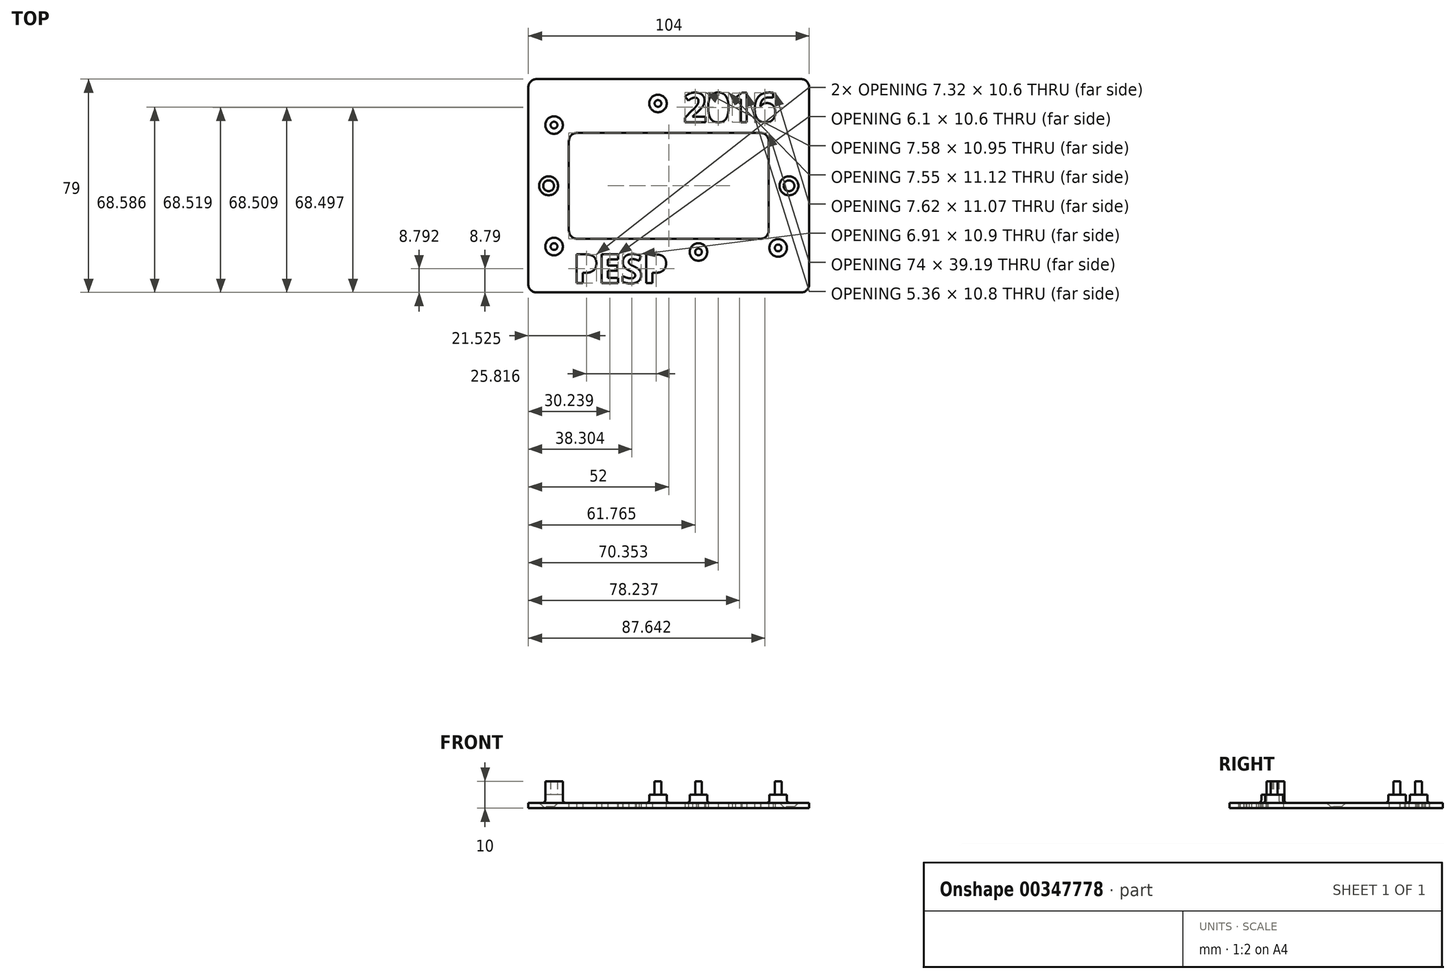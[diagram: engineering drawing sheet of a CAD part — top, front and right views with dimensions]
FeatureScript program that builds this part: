
annotation { "Feature Type Name" : "Feature", "Feature Type Description" : "" }
export const myFeature = defineFeature(function(context is Context, id is Id, definition is map)
    precondition{}
    {
        {
            var Q0;
            Q0=qCreatedBy(makeId("Top.planeOp"),FACE);
            var sketch = newSketch(context, id + "F0", { "sketchPlane" : qUnion([Q0])});
            skLineSegment(sketch, "E0.bottom", {"start": v(47, -34.5) * mm, "end": v(-47, -34.5) * mm});
            skLineSegment(sketch, "E0.top", {"start": v(47, 34.5) * mm, "end": v(-47, 34.5) * mm});
            skLineSegment(sketch, "E0.left", {"start": v(47, -34.5) * mm, "end": v(47, 34.5) * mm});
            skLineSegment(sketch, "E0.right", {"start": v(-47, -34.5) * mm, "end": v(-47, 34.5) * mm});
            skPoint(sketch, "E0.middle", {"position": v(0, 0) * mm});
            skLineSegment(sketch, "E1.0", {"start": v(52, 39.5) * mm, "end": v(-52, 39.5) * mm});
            skLineSegment(sketch, "E1.1", {"start": v(52, -39.5) * mm, "end": v(52, 39.5) * mm});
            skLineSegment(sketch, "E1.2", {"start": v(52, -39.5) * mm, "end": v(-52, -39.5) * mm});
            skLineSegment(sketch, "E1.3", {"start": v(-52, -39.5) * mm, "end": v(-52, 39.5) * mm});
            skCircle(sketch, "E2", {"center": v(-42.5, 22.5) * mm, "radius": 1.25 * mm});
            skCircle(sketch, "E3.MirrorC", {"center": v(-42.5, -22.5) * mm, "radius": 1.25 * mm});
            skCircle(sketch, "E4", {"center": v(-4, 30.5) * mm, "radius": 1.25 * mm});
            skCircle(sketch, "E5", {"center": v(40.5, -23) * mm, "radius": 1.25 * mm});
            skCircle(sketch, "E6", {"center": v(11, -24.5) * mm, "radius": 1.25 * mm});
            skCircle(sketch, "E7.0", {"center": v(-4, 30.5) * mm, "radius": 3.25 * mm});
            skCircle(sketch, "E8.0", {"center": v(-42.5, 22.5) * mm, "radius": 3.25 * mm});
            skCircle(sketch, "E9.0", {"center": v(11, -24.5) * mm, "radius": 3.25 * mm});
            skCircle(sketch, "E10.0", {"center": v(40.5, -23) * mm, "radius": 3.25 * mm});
            skCircle(sketch, "E11.MirrorC", {"center": v(-42.5, -22.5) * mm, "radius": 3.25 * mm});
            skLineSegment(sketch, "E12.bottom", {"start": v(-37, 19.6) * mm, "end": v(37, 19.6) * mm});
            skLineSegment(sketch, "E12.top", {"start": v(-37, -19.6) * mm, "end": v(37, -19.6) * mm});
            skLineSegment(sketch, "E12.left", {"start": v(-37, 19.6) * mm, "end": v(-37, -19.6) * mm});
            skLineSegment(sketch, "E12.right", {"start": v(37, 19.6) * mm, "end": v(37, -19.6) * mm});
            skText(sketch, "E13", { "text": "PESP", "fontName": "OpenSans-Bold.ttf"});
            skText(sketch, "E14", { "text": "2016", "fontName": "OpenSans-Bold.ttf"});
            skCircle(sketch, "E15", {"center": v(-44.5, 0) * mm, "radius": 2 * mm});
            skCircle(sketch, "E16.MirrorC", {"center": v(44.5, 0) * mm, "radius": 2 * mm});
            const initialGuessF0  = {"E13": [-0.03547, -0.03601, 1, 0, 0.01069], "E14": [0.0054, 0.02361, 1, 0, 0.01089]};
            skSetInitialGuess(sketch, initialGuessF0);
            skSolve(sketch);
        }
        {
            var Q0;
            Q0=makeQuery(id+"F0.imprint","IMPRINT",FACE,{"disambiguationData":[TD([[makeQuery(id+"F0.imprint","IMPRINT",EDGE,{"derivedFrom":sQuery(id+"F0.wireOp",EDGE,"E0.bottom")}),1.0]])]});
            var Q1;
            Q1=makeQuery(id+"F0.imprint","IMPRINT",FACE,{"disambiguationData":[TD([[makeQuery(id+"F0.imprint","IMPRINT",EDGE,{"derivedFrom":sQuery(id+"F0.wireOp",EDGE,"E0.bottom")}),-1.0]])]});
            var Q2;
            Q2=makeQuery(id+"F0.imprint","IMPRINT",FACE,{"disambiguationData":[TD([[makeQuery(id+"F0.imprint","IMPRINT",EDGE,{"derivedFrom":sQuery(id+"F0.wireOp",EDGE,"E4")}),-1.0]])]});
            var Q3;
            Q3=makeQuery(id+"F0.imprint","IMPRINT",FACE,{"disambiguationData":[TD([[makeQuery(id+"F0.imprint","IMPRINT",EDGE,{"derivedFrom":sQuery(id+"F0.wireOp",EDGE,"E4")}),1.0]])]});
            var Q4;
            Q4=makeQuery(id+"F0.imprint","IMPRINT",FACE,{"disambiguationData":[TD([[makeQuery(id+"F0.imprint","IMPRINT",EDGE,{"derivedFrom":sQuery(id+"F0.wireOp",EDGE,"E5")}),1.0]])]});
            var Q5;
            Q5=makeQuery(id+"F0.imprint","IMPRINT",FACE,{"disambiguationData":[TD([[makeQuery(id+"F0.imprint","IMPRINT",EDGE,{"derivedFrom":sQuery(id+"F0.wireOp",EDGE,"E5")}),-1.0]])]});
            var Q6;
            Q6=makeQuery(id+"F0.imprint","IMPRINT",FACE,{"disambiguationData":[TD([[makeQuery(id+"F0.imprint","IMPRINT",EDGE,{"derivedFrom":sQuery(id+"F0.wireOp",EDGE,"E6")}),1.0]])]});
            var Q7;
            Q7=makeQuery(id+"F0.imprint","IMPRINT",FACE,{"disambiguationData":[TD([[makeQuery(id+"F0.imprint","IMPRINT",EDGE,{"derivedFrom":sQuery(id+"F0.wireOp",EDGE,"E6")}),-1.0]])]});
            var Q8;
            Q8=makeQuery(id+"F0.imprint","IMPRINT",FACE,{"disambiguationData":[TD([[makeQuery(id+"F0.imprint","IMPRINT",EDGE,{"derivedFrom":sQuery(id+"F0.wireOp",EDGE,"E3.MirrorC")}),-1.0]])]});
            var Q9;
            Q9=makeQuery(id+"F0.imprint","IMPRINT",FACE,{"disambiguationData":[TD([[makeQuery(id+"F0.imprint","IMPRINT",EDGE,{"derivedFrom":sQuery(id+"F0.wireOp",EDGE,"E3.MirrorC")}),1.0]])]});
            var Q10;
            Q10=makeQuery(id+"F0.imprint","IMPRINT",FACE,{"disambiguationData":[TD([[makeQuery(id+"F0.imprint","IMPRINT",EDGE,{"derivedFrom":sQuery(id+"F0.wireOp",EDGE,"E2")}),-1.0]])]});
            var Q11;
            Q11=makeQuery(id+"F0.imprint","IMPRINT",FACE,{"disambiguationData":[TD([[makeQuery(id+"F0.imprint","IMPRINT",EDGE,{"derivedFrom":sQuery(id+"F0.wireOp",EDGE,"E2")}),1.0]])]});
            extrude(context, id + "F1", {"entities" : qUnion([Q0, Q1, Q2, Q3, Q4, Q5, Q6, Q7, Q8, Q9, Q10, Q11]), "depth" : 2 * mm});
        }
        {
            var Q0;
            Q0=makeQuery(id+"F0.imprint","IMPRINT",FACE,{"disambiguationData":[TD([[makeQuery(id+"F0.imprint","IMPRINT",EDGE,{"derivedFrom":sQuery(id+"F0.wireOp",EDGE,"E4")}),1.0]])]});
            var Q1;
            Q1=makeQuery(id+"F0.imprint","IMPRINT",FACE,{"disambiguationData":[TD([[makeQuery(id+"F0.imprint","IMPRINT",EDGE,{"derivedFrom":sQuery(id+"F0.wireOp",EDGE,"E4")}),-1.0]])]});
            var Q2;
            Q2=makeQuery(id+"F0.imprint","IMPRINT",FACE,{"disambiguationData":[TD([[makeQuery(id+"F0.imprint","IMPRINT",EDGE,{"derivedFrom":sQuery(id+"F0.wireOp",EDGE,"E3.MirrorC")}),-1.0]])]});
            var Q3;
            Q3=makeQuery(id+"F0.imprint","IMPRINT",FACE,{"disambiguationData":[TD([[makeQuery(id+"F0.imprint","IMPRINT",EDGE,{"derivedFrom":sQuery(id+"F0.wireOp",EDGE,"E3.MirrorC")}),1.0]])]});
            var Q4;
            Q4=makeQuery(id+"F0.imprint","IMPRINT",FACE,{"disambiguationData":[TD([[makeQuery(id+"F0.imprint","IMPRINT",EDGE,{"derivedFrom":sQuery(id+"F0.wireOp",EDGE,"E6")}),1.0]])]});
            var Q5;
            Q5=makeQuery(id+"F0.imprint","IMPRINT",FACE,{"disambiguationData":[TD([[makeQuery(id+"F0.imprint","IMPRINT",EDGE,{"derivedFrom":sQuery(id+"F0.wireOp",EDGE,"E6")}),-1.0]])]});
            var Q6;
            Q6=makeQuery(id+"F0.imprint","IMPRINT",FACE,{"disambiguationData":[TD([[makeQuery(id+"F0.imprint","IMPRINT",EDGE,{"derivedFrom":sQuery(id+"F0.wireOp",EDGE,"E5")}),1.0]])]});
            var Q7;
            Q7=makeQuery(id+"F0.imprint","IMPRINT",FACE,{"disambiguationData":[TD([[makeQuery(id+"F0.imprint","IMPRINT",EDGE,{"derivedFrom":sQuery(id+"F0.wireOp",EDGE,"E5")}),-1.0]])]});
            var Q8;
            Q8=makeQuery(id+"F0.imprint","IMPRINT",FACE,{"disambiguationData":[TD([[makeQuery(id+"F0.imprint","IMPRINT",EDGE,{"derivedFrom":sQuery(id+"F0.wireOp",EDGE,"E2")}),-1.0]])]});
            var Q9;
            Q9=makeQuery(id+"F0.imprint","IMPRINT",FACE,{"disambiguationData":[TD([[makeQuery(id+"F0.imprint","IMPRINT",EDGE,{"derivedFrom":sQuery(id+"F0.wireOp",EDGE,"E2")}),1.0]])]});
            extrude(context, id + "F2", {"entities" : qUnion([Q0, Q1, Q2, Q3, Q4, Q5, Q6, Q7, Q8, Q9]), "operationType" : NewBodyOperationType.ADD, "depth" : 5 * mm});
        }
        {
            var Q0;
            Q0=makeQuery(id+"F0.imprint","IMPRINT",FACE,{"disambiguationData":[TD([[makeQuery(id+"F0.imprint","IMPRINT",EDGE,{"derivedFrom":sQuery(id+"F0.wireOp",EDGE,"E4")}),1.0]])]});
            var Q1;
            Q1=makeQuery(id+"F0.imprint","IMPRINT",FACE,{"disambiguationData":[TD([[makeQuery(id+"F0.imprint","IMPRINT",EDGE,{"derivedFrom":sQuery(id+"F0.wireOp",EDGE,"E2")}),1.0]])]});
            var Q2;
            Q2=makeQuery(id+"F0.imprint","IMPRINT",FACE,{"disambiguationData":[TD([[makeQuery(id+"F0.imprint","IMPRINT",EDGE,{"derivedFrom":sQuery(id+"F0.wireOp",EDGE,"E3.MirrorC")}),-1.0]])]});
            var Q3;
            Q3=makeQuery(id+"F0.imprint","IMPRINT",FACE,{"disambiguationData":[TD([[makeQuery(id+"F0.imprint","IMPRINT",EDGE,{"derivedFrom":sQuery(id+"F0.wireOp",EDGE,"E6")}),1.0]])]});
            var Q4;
            Q4=makeQuery(id+"F0.imprint","IMPRINT",FACE,{"disambiguationData":[TD([[makeQuery(id+"F0.imprint","IMPRINT",EDGE,{"derivedFrom":sQuery(id+"F0.wireOp",EDGE,"E5")}),1.0]])]});
            extrude(context, id + "F3", {"entities" : qUnion([Q0, Q1, Q2, Q3, Q4]), "operationType" : NewBodyOperationType.ADD, "depth" : 10 * mm});
        }
        {
            var Q0;
            Q0=makeQuery(id+"F1.opExtrude","SWEPT_EDGE",EDGE,{"disambiguationData":[OSD([sQuery(id+"F0.wireOp",EDGE,"E12.bottom"),sQuery(id+"F0.wireOp",EDGE,"E12.left")])]});
            var Q1;
            Q1=makeQuery(id+"F1.opExtrude","SWEPT_EDGE",EDGE,{"disambiguationData":[OSD([sQuery(id+"F0.wireOp",EDGE,"E12.bottom"),sQuery(id+"F0.wireOp",EDGE,"E12.right")])]});
            var Q2;
            Q2=makeQuery(id+"F1.opExtrude","SWEPT_EDGE",EDGE,{"disambiguationData":[OSD([sQuery(id+"F0.wireOp",EDGE,"E12.top"),sQuery(id+"F0.wireOp",EDGE,"E12.left")])]});
            var Q3;
            Q3=makeQuery(id+"F1.opExtrude","SWEPT_EDGE",EDGE,{"disambiguationData":[OSD([sQuery(id+"F0.wireOp",EDGE,"E12.top"),sQuery(id+"F0.wireOp",EDGE,"E12.right")])]});
            var Q4;
            Q4=makeQuery(id+"F1.opExtrude","SWEPT_EDGE",EDGE,{"disambiguationData":[OSD([sQuery(id+"F0.wireOp",EDGE,"E1.0"),sQuery(id+"F0.wireOp",EDGE,"E1.1")])]});
            var Q5;
            Q5=makeQuery(id+"F1.opExtrude","SWEPT_EDGE",EDGE,{"disambiguationData":[OSD([sQuery(id+"F0.wireOp",EDGE,"E1.1"),sQuery(id+"F0.wireOp",EDGE,"E1.2")])]});
            var Q6;
            Q6=makeQuery(id+"F1.opExtrude","SWEPT_EDGE",EDGE,{"disambiguationData":[OSD([sQuery(id+"F0.wireOp",EDGE,"E1.0"),sQuery(id+"F0.wireOp",EDGE,"E1.3")])]});
            var Q7;
            Q7=makeQuery(id+"F1.opExtrude","SWEPT_EDGE",EDGE,{"disambiguationData":[OSD([sQuery(id+"F0.wireOp",EDGE,"E1.2"),sQuery(id+"F0.wireOp",EDGE,"E1.3")])]});
            fillet(context, id + "F4", {"entities" : qUnion([Q0, Q1, Q2, Q3, Q4, Q5, Q6, Q7]), "radius" : 3 * mm, "tangentPropagation" : true, "allowEdgeOverflow" : false});
        }
        {
            var Q0;
            Q0=makeQuery(id+"F2.boolean.opBoolean","INTERSECT",EDGE,{"derivedFrom":[makeQuery(id+"F1.opExtrude","CAP_FACE",FACE,{"disambiguationData":[OSD([sQuery(id+"F0.wireOp",EDGE,"E1.0"),sQuery(id+"F0.wireOp",EDGE,"E1.1"),sQuery(id+"F0.wireOp",EDGE,"E1.2"),sQuery(id+"F0.wireOp",EDGE,"E1.3"),sQuery(id+"F0.wireOp",EDGE,"E12.bottom"),sQuery(id+"F0.wireOp",EDGE,"E12.top"),sQuery(id+"F0.wireOp",EDGE,"E12.left"),sQuery(id+"F0.wireOp",EDGE,"E12.right")])],"isStart":false}),makeQuery(id+"F2.opExtrude","SWEPT_FACE",FACE,{"disambiguationData":[OSD([sQuery(id+"F0.wireOp",EDGE,"E8.0")])]})]});
            var Q1;
            Q1=makeQuery(id+"F2.boolean.opBoolean","INTERSECT",EDGE,{"derivedFrom":[makeQuery(id+"F1.opExtrude","CAP_FACE",FACE,{"disambiguationData":[OSD([sQuery(id+"F0.wireOp",EDGE,"E1.0"),sQuery(id+"F0.wireOp",EDGE,"E1.1"),sQuery(id+"F0.wireOp",EDGE,"E1.2"),sQuery(id+"F0.wireOp",EDGE,"E1.3"),sQuery(id+"F0.wireOp",EDGE,"E12.bottom"),sQuery(id+"F0.wireOp",EDGE,"E12.top"),sQuery(id+"F0.wireOp",EDGE,"E12.left"),sQuery(id+"F0.wireOp",EDGE,"E12.right")])],"isStart":false}),makeQuery(id+"F2.opExtrude","SWEPT_FACE",FACE,{"disambiguationData":[OSD([sQuery(id+"F0.wireOp",EDGE,"E11.MirrorC")])]})]});
            var Q2;
            Q2=makeQuery(id+"F2.boolean.opBoolean","INTERSECT",EDGE,{"derivedFrom":[makeQuery(id+"F1.opExtrude","CAP_FACE",FACE,{"disambiguationData":[OSD([sQuery(id+"F0.wireOp",EDGE,"E1.0"),sQuery(id+"F0.wireOp",EDGE,"E1.1"),sQuery(id+"F0.wireOp",EDGE,"E1.2"),sQuery(id+"F0.wireOp",EDGE,"E1.3"),sQuery(id+"F0.wireOp",EDGE,"E12.bottom"),sQuery(id+"F0.wireOp",EDGE,"E12.top"),sQuery(id+"F0.wireOp",EDGE,"E12.left"),sQuery(id+"F0.wireOp",EDGE,"E12.right")])],"isStart":false}),makeQuery(id+"F2.opExtrude","SWEPT_FACE",FACE,{"disambiguationData":[OSD([sQuery(id+"F0.wireOp",EDGE,"E9.0")])]})]});
            var Q3;
            Q3=makeQuery(id+"F2.boolean.opBoolean","INTERSECT",EDGE,{"derivedFrom":[makeQuery(id+"F1.opExtrude","CAP_FACE",FACE,{"disambiguationData":[OSD([sQuery(id+"F0.wireOp",EDGE,"E1.0"),sQuery(id+"F0.wireOp",EDGE,"E1.1"),sQuery(id+"F0.wireOp",EDGE,"E1.2"),sQuery(id+"F0.wireOp",EDGE,"E1.3"),sQuery(id+"F0.wireOp",EDGE,"E12.bottom"),sQuery(id+"F0.wireOp",EDGE,"E12.top"),sQuery(id+"F0.wireOp",EDGE,"E12.left"),sQuery(id+"F0.wireOp",EDGE,"E12.right")])],"isStart":false}),makeQuery(id+"F2.opExtrude","SWEPT_FACE",FACE,{"disambiguationData":[OSD([sQuery(id+"F0.wireOp",EDGE,"E10.0")])]})]});
            var Q4;
            Q4=makeQuery(id+"F2.boolean.opBoolean","INTERSECT",EDGE,{"derivedFrom":[makeQuery(id+"F1.opExtrude","CAP_FACE",FACE,{"disambiguationData":[OSD([sQuery(id+"F0.wireOp",EDGE,"E1.0"),sQuery(id+"F0.wireOp",EDGE,"E1.1"),sQuery(id+"F0.wireOp",EDGE,"E1.2"),sQuery(id+"F0.wireOp",EDGE,"E1.3"),sQuery(id+"F0.wireOp",EDGE,"E12.bottom"),sQuery(id+"F0.wireOp",EDGE,"E12.top"),sQuery(id+"F0.wireOp",EDGE,"E12.left"),sQuery(id+"F0.wireOp",EDGE,"E12.right")])],"isStart":false}),makeQuery(id+"F2.opExtrude","SWEPT_FACE",FACE,{"disambiguationData":[OSD([sQuery(id+"F0.wireOp",EDGE,"E7.0")])]})]});
            fillet(context, id + "F5", {"entities" : qUnion([Q0, Q1, Q2, Q3, Q4]), "radius" : 1 * mm, "tangentPropagation" : true, "allowEdgeOverflow" : false});
        }
        {
            var Q0;
            Q0=makeQuery(id+"F1.opExtrude","CAP_EDGE",EDGE,{"disambiguationData":[OSD([sQuery(id+"F0.wireOp",EDGE,"E15")])],"isStart":false});
            var Q1;
            Q1=makeQuery(id+"F1.opExtrude","CAP_EDGE",EDGE,{"disambiguationData":[OSD([sQuery(id+"F0.wireOp",EDGE,"E16.MirrorC")])],"isStart":false});
            chamfer(context, id + "F6", {"entities" : qUnion([Q0, Q1]), "width" : 1.5 * mm, "tangentPropagation" : true});
        }
    });
